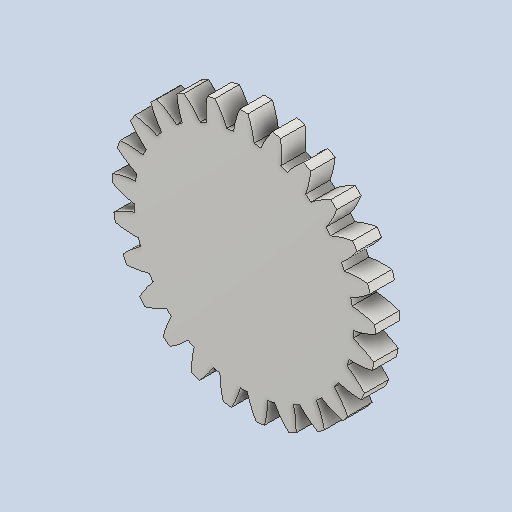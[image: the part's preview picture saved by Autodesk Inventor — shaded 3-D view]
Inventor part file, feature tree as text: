
AUTODESK INVENTOR PART (.ipt)
format: ipt  version: 2024 (Build 280153000, 153)  size: 245,760 bytes
history: native  units: mm (DEFAULTED — no unit token found)
features: plane x3, other x3, extrude x1, sketch x1
ambient origin geometry x8: Origin, YZ Plane, XZ Plane, XY Plane, X Axis, Y Axis, Z Axis, Center Point
bodies: Solid1 (feature_tree)
feature tree (8):
  extrude  "Extrusion1"  Depth=5.0mm TaperAngle=0.0deg
  plane  "Work Plane2"
  plane  "Work Plane8"
  plane  "Work Plane9"
  other  "Spur Gear"
  sketch  "Sketch1"  dims[d0=54.0mm d1=5.0mm d2=0.0mm d3=50.0mm d4=10.0mm d5=0.0mm d16=35.0mm d17=0.0mm d34=1.256637mm d39=0.0mm d41=0.0mm d43=35.0mm d46=35.0mm d47=0.0mm d48=0.0mm]
  other  "Srf1"
  other  "Pitch Diameter"
